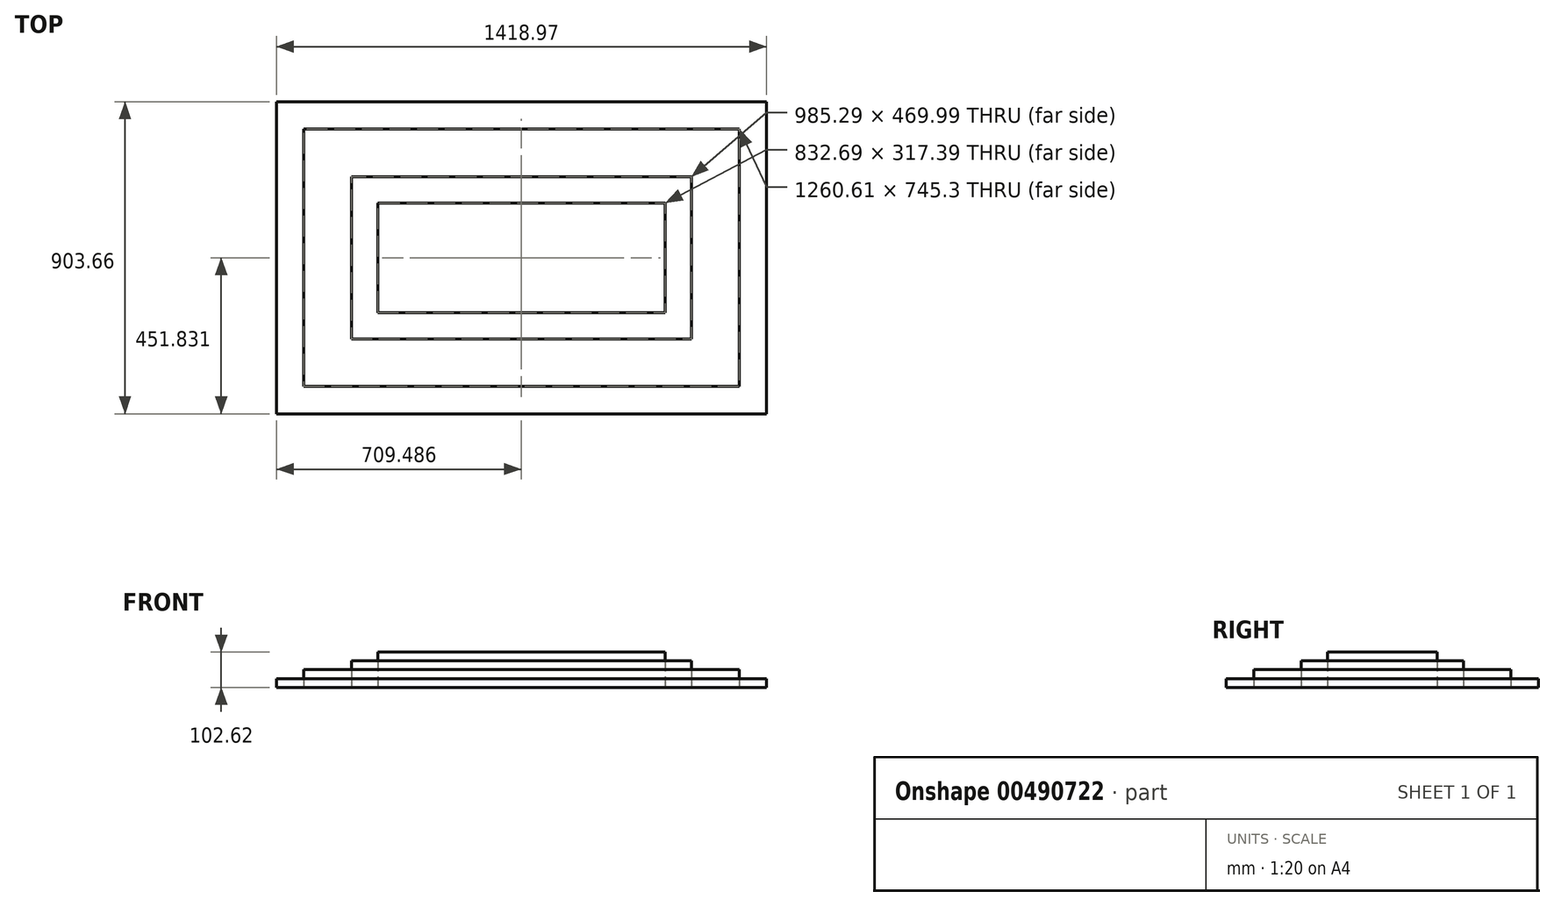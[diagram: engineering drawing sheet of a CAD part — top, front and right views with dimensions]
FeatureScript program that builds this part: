
annotation { "Feature Type Name" : "Feature", "Feature Type Description" : "" }
export const myFeature = defineFeature(function(context is Context, id is Id, definition is map)
    precondition{}
    {
        {
            var Q0;
            Q0=qCreatedBy(makeId("Top.planeOp"),FACE);
            var sketch = newSketch(context, id + "F0", { "sketchPlane" : qUnion([Q0])});
            skLineSegment(sketch, "E0", {"start": v(0, 0) * mm, "end": v(905.09, -890.9) * mm, "construction": true});
            skLineSegment(sketch, "E1.bottom", {"start": v(1321.43, -732.22) * mm, "end": v(488.74, -732.22) * mm});
            skLineSegment(sketch, "E1.top", {"start": v(1321.43, -1049.6) * mm, "end": v(488.74, -1049.6) * mm});
            skLineSegment(sketch, "E1.left", {"start": v(1321.43, -732.22) * mm, "end": v(1321.43, -1049.6) * mm});
            skLineSegment(sketch, "E1.right", {"start": v(488.74, -732.22) * mm, "end": v(488.74, -1049.6) * mm});
            skPoint(sketch, "E1.middle", {"position": v(905.09, -890.9) * mm});
            skLineSegment(sketch, "E2.0", {"start": v(412.44, -655.92) * mm, "end": v(412.44, -1125.9) * mm});
            skLineSegment(sketch, "E2.1", {"start": v(1397.73, -655.92) * mm, "end": v(412.44, -655.92) * mm});
            skLineSegment(sketch, "E2.2", {"start": v(1397.73, -655.92) * mm, "end": v(1397.73, -1125.9) * mm});
            skLineSegment(sketch, "E2.3", {"start": v(1397.73, -1125.9) * mm, "end": v(412.44, -1125.9) * mm});
            skLineSegment(sketch, "E3.0", {"start": v(1535.4, -1263.56) * mm, "end": v(274.78, -1263.56) * mm});
            skLineSegment(sketch, "E3.1", {"start": v(1535.4, -518.26) * mm, "end": v(1535.4, -1263.56) * mm});
            skLineSegment(sketch, "E3.2", {"start": v(1535.4, -518.26) * mm, "end": v(274.78, -518.26) * mm});
            skLineSegment(sketch, "E3.3", {"start": v(274.78, -518.26) * mm, "end": v(274.78, -1263.56) * mm});
            skLineSegment(sketch, "E4.0", {"start": v(1614.57, -439.08) * mm, "end": v(1614.57, -1342.74) * mm});
            skLineSegment(sketch, "E4.1", {"start": v(1614.57, -439.08) * mm, "end": v(195.6, -439.08) * mm});
            skLineSegment(sketch, "E4.2", {"start": v(195.6, -439.08) * mm, "end": v(195.6, -1342.74) * mm});
            skLineSegment(sketch, "E4.3", {"start": v(1614.57, -1342.74) * mm, "end": v(195.6, -1342.74) * mm});
            skLineSegment(sketch, "E5.0", {"start": v(1752.24, -1480.4) * mm, "end": v(195.6, -1480.4) * mm});
            skLineSegment(sketch, "E5.1", {"start": v(1752.24, -301.41) * mm, "end": v(1752.24, -1480.4) * mm});
            skLineSegment(sketch, "E5.2", {"start": v(1752.24, -301.41) * mm, "end": v(195.6, -301.41) * mm});
            skSolve(sketch);
        }
        {
            var Q0;
            Q0=makeQuery(id+"F0.imprint","IMPRINT",FACE,{"disambiguationData":[TD([[makeQuery(id+"F0.imprint","IMPRINT",EDGE,{"derivedFrom":sQuery(id+"F0.wireOp",EDGE,"E3.0")}),1.0]])]});
            extrude(context, id + "F1", {"entities" : qUnion([Q0]), "depth" : 25.4 * mm});
        }
        {
            var Q0;
            Q0=makeQuery(id+"F0.imprint","IMPRINT",FACE,{"disambiguationData":[TD([[makeQuery(id+"F0.imprint","IMPRINT",EDGE,{"derivedFrom":sQuery(id+"F0.wireOp",EDGE,"E2.0")}),-1.0]])]});
            extrude(context, id + "F2", {"entities" : qUnion([Q0]), "depth" : 51.3 * mm});
        }
        {
            var Q0;
            Q0=makeQuery(id+"F0.imprint","IMPRINT",FACE,{"disambiguationData":[TD([[makeQuery(id+"F0.imprint","IMPRINT",EDGE,{"derivedFrom":sQuery(id+"F0.wireOp",EDGE,"E1.bottom")}),-1.0]])]});
            extrude(context, id + "F3", {"entities" : qUnion([Q0]), "depth" : 76.96 * mm});
        }
        {
            var Q0;
            Q0=makeQuery(id+"F0.imprint","IMPRINT",FACE,{"disambiguationData":[TD([[makeQuery(id+"F0.imprint","IMPRINT",EDGE,{"derivedFrom":sQuery(id+"F0.wireOp",EDGE,"E1.bottom")}),1.0]])]});
            extrude(context, id + "F4", {"entities" : qUnion([Q0]), "depth" : 102.62 * mm});
        }
    });
